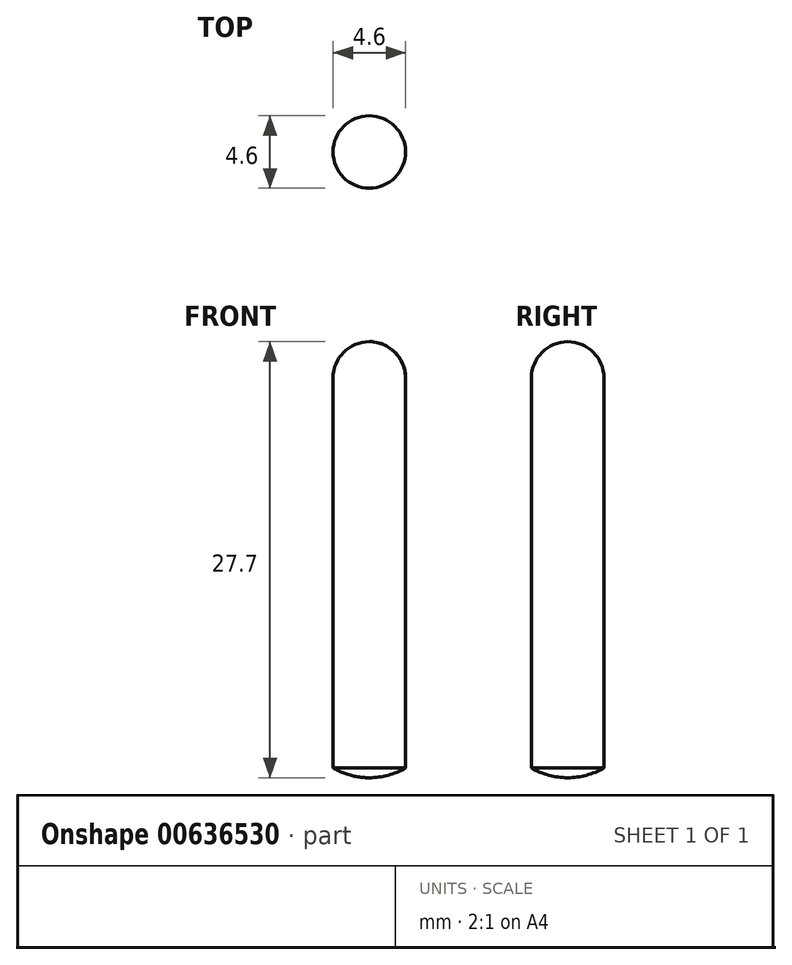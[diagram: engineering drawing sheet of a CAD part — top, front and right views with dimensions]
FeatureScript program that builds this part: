
annotation { "Feature Type Name" : "Feature", "Feature Type Description" : "" }
export const myFeature = defineFeature(function(context is Context, id is Id, definition is map)
    precondition{}
    {
        {
            var Q0;
            Q0=qCreatedBy(makeId("Front.planeOp"),FACE);
            var sketch = newSketch(context, id + "F0", { "sketchPlane" : qUnion([Q0])});
            skLineSegment(sketch, "E0", {"start": v(0, 0) * mm, "end": v(0, -20.8) * mm});
            skArc(sketch, "E1", {"start": v(2.3, 0) * mm, "mid": v(1.63, 1.63) * mm, "end": v(0, 2.3) * mm});
            skArc(sketch, "E2", {"start": v(0, -25.4) * mm, "mid": v(1.2, -25.24) * mm, "end": v(2.3, -24.78) * mm});
            skLineSegment(sketch, "E3", {"start": v(2.3, 0) * mm, "end": v(2.3, -24.78) * mm});
            skLineSegment(sketch, "E4", {"start": v(0, 0) * mm, "end": v(0, 2.3) * mm});
            skLineSegment(sketch, "E5", {"start": v(0, -20.8) * mm, "end": v(0, -25.4) * mm});
            skSolve(sketch);
        }
        {
            var Q0;
            Q0=qCreatedBy(makeId("Front.planeOp"),FACE);
            var sketch = newSketch(context, id + "F1", { "sketchPlane" : qUnion([Q0])});
            skLineSegment(sketch, "E6", {"start": v(0, 28.92) * mm, "end": v(0, -46.56) * mm});
            skSolve(sketch);
        }
        {
            var Q0;
            Q0 = qSketchRegion(id + "F0", true);
            var Q1;
            Q1=sQuery(id+"F1.wireOp",EDGE,"E6");
            revolve(context, id + "F2", {"entities" : qUnion([Q0]), "axis" : qUnion([Q1]), "revolveType" : RevolveType.FULL});
        }
    });
